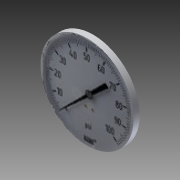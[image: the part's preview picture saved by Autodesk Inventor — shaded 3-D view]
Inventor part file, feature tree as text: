
AUTODESK INVENTOR PART (.ipt)
format: ipt  version: 2011 (Build 150239000, 239)  size: 118,784 bytes
history: native  units: in
note: dims shown in document units (in); Inventor stores cm internally (conversion verified against a paired STEP export)
features: other x2, sketch x2, extrude x1
ambient origin geometry x8: Origin, YZ Plane, XZ Plane, XY Plane, X Axis, Y Axis, Z Axis, Center Point
bodies: Solid1 (feature_tree)
feature tree (5):
  extrude  "Extrusion1"  Depth=0.1in TaperAngle=0.0deg
  other  "Decal1"
  sketch  "Sketch1"  dims[d0=1.525in d1=0.1in d2=0.0in]
  sketch  "Sketch2"
  other  "Image2"
